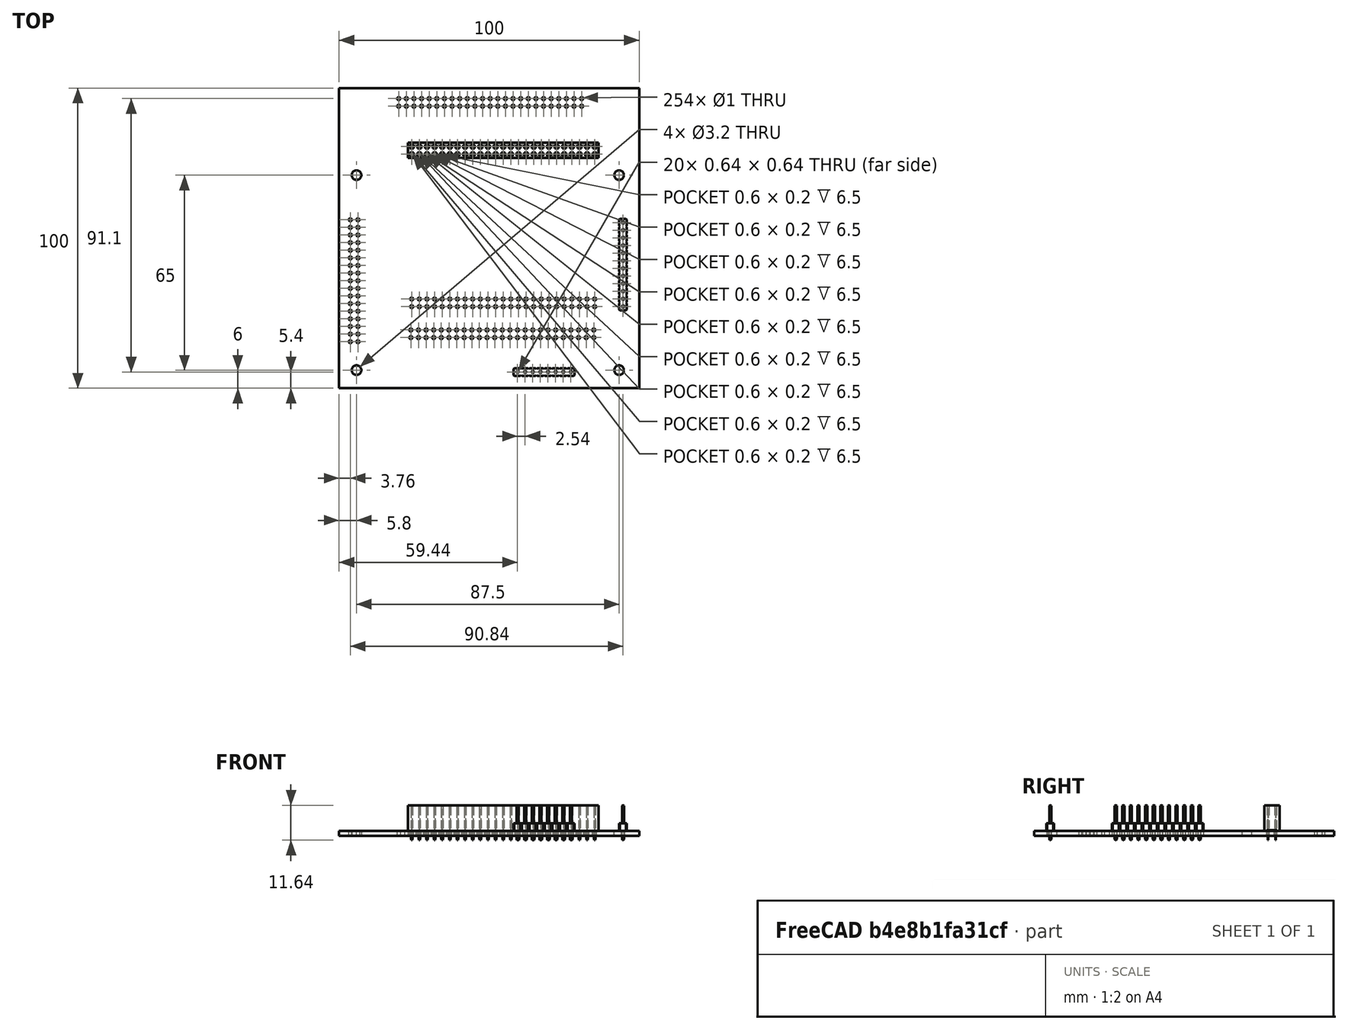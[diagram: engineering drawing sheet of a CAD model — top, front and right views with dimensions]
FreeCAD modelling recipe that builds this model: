
FCSTD DOCUMENT  (FreeCAD 1.0R39109 (Git))
Label: fpga_ext_board
License: All rights reserved
LicenseURL: https://en.wikipedia.org/wiki/All_rights_reserved
objects: Part::Feature×4, App::Part×4, App::Link×3, PartDesign::CoordinateSystem×1, Sketcher::SketchObject×1
note: 7 computed .brp shape members not serialized (recipe doc carries the construction recipe); baked Part::Feature solids carry a one-line shape summary decoded from their .brp

FEATURE [PartDesign::CoordinateSystem] Local_CS_e45
  AttacherType = Attacher::AttachEngine3D
  MapMode = 2
FEATURE [Part::Feature] Pcb_e45
  shape: bbox 100 x 100 x 1.6 mm, 264 faces (baked)
FEATURE [Sketcher::SketchObject] PCB_Sketch_e45
  ArcFitTolerance = 1e-06
  FullyConstrained = false
  MakeInternals = false
  sketch-geometry (4):
    g0: LineSegment StartX=56.7 StartY=-51 StartZ=0 EndX=156.7 EndY=-51 EndZ=0
    g1: LineSegment StartX=156.7 StartY=-51 StartZ=0 EndX=156.7 EndY=-151 EndZ=0
    g2: LineSegment StartX=156.7 StartY=-151 StartZ=0 EndX=56.7 EndY=-151 EndZ=0
    g3: LineSegment StartX=56.7 StartY=-151 StartZ=0 EndX=56.7 EndY=-51 EndZ=0
  constraints (4):
    c: Coincident(g2,g3)
    c: Coincident(g0,g3)
    c: Coincident(g1,g2)
    c: Coincident(g0,g1)
FEATURE [App::Part] Board_Geoms_e45
  Group = -> [Pcb_e45,PCB_Sketch_e45]
  Origin = -> Origin
FEATURE [Part::Feature] Shape  label="J3_PinSocket_2x25_P2.54mm_Vertical_5b0326eaf643"
  Placement = pos=(80.9,-70.5,0) rot=(0,0,1;1.5708rad)
  shape: bbox 63.5 x 5.08 x 11.6 mm, 1310 faces (baked)
FEATURE [App::Link] J3_PinSocket_2x25_P2_54mm_Vertical_5b0326eaf643_ln_  label="J1_PinSocket_2x25_P2.54mm_Vertical_5e9946493b34"
  LinkPlacement = pos=(80.6,-131.6,0) rot=(0,0,1;1.5708rad)
  LinkedObject = -> Shape
  Placement = pos=(80.6,-131.6,0) rot=(0,0,1;1.5708rad)
FEATURE [App::Link] J3_PinSocket_2x25_P2_54mm_Vertical_5b0326eaf643_ln_001  label="J4_PinSocket_2x25_P2.54mm_Vertical_c0175bcf8e3d"
  LinkPlacement = pos=(76.56,-54.5,0) rot=(0,0,1;1.5708rad)
  LinkedObject = -> Shape
  Placement = pos=(76.56,-54.5,0) rot=(0,0,1;1.5708rad)
FEATURE [Part::Feature] Shape001  label="J6_PinHeader_1x08_P254mm_Vertical_e00167c7260b"
  Placement = pos=(116.14,-145.6,0) rot=(0,0,1;1.5708rad)
  shape: bbox 20.32 x 2.54 x 11.54 mm, 196 faces (baked)
FEATURE [Part::Feature] Shape002  label="J7_PinHeader_1x12_P254mm_Vertical_57171d797b48"
  Placement = pos=(151.3,-95.84,0) rot=(0,0,1;0rad)
  shape: bbox 2.54 x 30.48 x 11.54 mm, 292 faces (baked)
FEATURE [App::Link] J3_PinSocket_2x25_P2_54mm_Vertical_5b0326eaf643_ln_002  label="J2_PinSocket_2x25_P2.54mm_Vertical_ab23b89833e9"
  LinkPlacement = pos=(80.9,-121.3,0) rot=(0,0,1;1.5708rad)
  LinkedObject = -> Shape
  Placement = pos=(80.9,-121.3,0) rot=(0,0,1;1.5708rad)
FEATURE [App::Part] Top_e45
  Group = -> [Shape,J3_PinSocket_2x25_P2_54mm_Vertical_5b0326eaf643_ln_,J3_PinSocket_2x25_P2_54mm_Vertical_5b0326eaf643_ln_001,Shape001,Shape002,J3_PinSocket_2x25_P2_54mm_Vertical_5b0326eaf643_ln_002]
  Origin = -> Origin003
FEATURE [App::Part] Step_Models_e45
  Group = -> [Top_e45]
  Origin = -> Origin002
FEATURE [App::Part] Board_e45  label="fpga_ext_board"
  Group = -> [Local_CS_e45,Board_Geoms_e45,Step_Models_e45]
  Origin = -> Origin001
